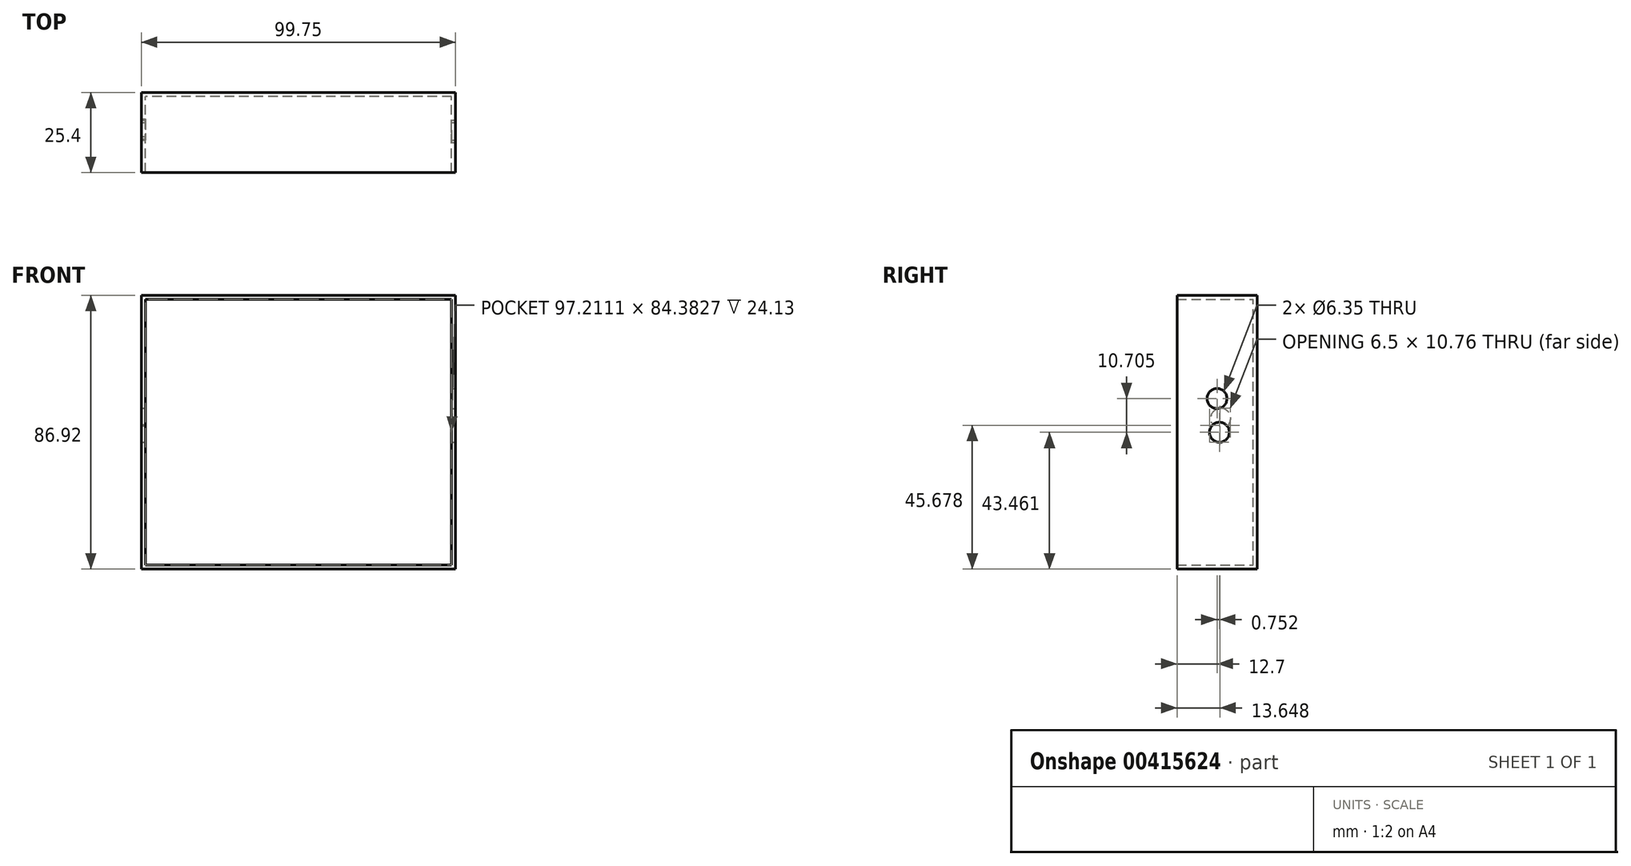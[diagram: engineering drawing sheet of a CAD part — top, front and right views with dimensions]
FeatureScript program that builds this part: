
annotation { "Feature Type Name" : "Feature", "Feature Type Description" : "" }
export const myFeature = defineFeature(function(context is Context, id is Id, definition is map)
    precondition{}
    {
        {
            var Q0;
            Q0=qCreatedBy(makeId("Front.planeOp"),FACE);
            var sketch = newSketch(context, id + "F0", { "sketchPlane" : qUnion([Q0])});
            skLineSegment(sketch, "E0.bottom", {"start": v(99.75, 0) * mm, "end": v(0, 0) * mm});
            skLineSegment(sketch, "E0.top", {"start": v(99.75, 86.92) * mm, "end": v(0, 86.92) * mm});
            skLineSegment(sketch, "E0.left", {"start": v(99.75, 0) * mm, "end": v(99.75, 86.92) * mm});
            skLineSegment(sketch, "E0.right", {"start": v(0, 0) * mm, "end": v(0, 86.92) * mm});
            skSolve(sketch);
        }
        {
            var Q0;
            Q0=makeQuery(id+"F0.imprint","IMPRINT",FACE,{"disambiguationData":[TD([[makeQuery(id+"F0.imprint","IMPRINT",EDGE,{"derivedFrom":sQuery(id+"F0.wireOp",EDGE,"E0.bottom")}),-1.0]])]});
            extrude(context, id + "F1", {"entities" : qUnion([Q0]), "depth" : 25.4 * mm});
        }
        {
            var Q0;
            Q0=makeQuery(id+"F1.opExtrude","CAP_FACE",FACE,{"disambiguationData":[OSD([sQuery(id+"F0.wireOp",EDGE,"E0.bottom"),sQuery(id+"F0.wireOp",EDGE,"E0.top"),sQuery(id+"F0.wireOp",EDGE,"E0.left"),sQuery(id+"F0.wireOp",EDGE,"E0.right")])],"isStart":false});
            shell(context, id + "F2", {"entities" : qUnion([Q0]), "thickness" : 1.27 * mm});
        }
        {
            var Q0;
            Q0=makeQuery(id+"F1.opExtrude","SWEPT_FACE",FACE,{"disambiguationData":[OSD([sQuery(id+"F0.wireOp",EDGE,"E0.left")])]});
            var sketch = newSketch(context, id + "F3", { "sketchPlane" : qUnion([Q0])});
            skPoint(sketch, "E1", {"position": v(-11.95, 43.46) * mm});
            skPoint(sketch, "E1.positionSnap0", {"position": v(0, 43.46) * mm});
            skSolve(sketch);
        }
        {
            var Q0;
            Q0=sQuery(id+"F3.wireOp",VERTEX,"E1");
            var Q1;
            Q1=makeQuery(id+"F1.opExtrude","SWEPT_BODY",BODY,{"disambiguationData":[OSD([sQuery(id+"F0.wireOp",EDGE,"E0.bottom"),sQuery(id+"F0.wireOp",EDGE,"E0.top"),sQuery(id+"F0.wireOp",EDGE,"E0.left"),sQuery(id+"F0.wireOp",EDGE,"E0.right")])]});
            hole(context, id + "F4", {"style" : HoleStyle.SIMPLE, "endStyle" : HoleEndStyle.THROUGH, "holeDiameter" : 6.35 * mm, "isTappedThrough" : true, "tappedDepth" : 12.7 * mm, "tapClearance" : 3, "locations" : qUnion([Q0]), "scope" : qUnion([Q1])});
        }
        {
            var Q0;
            Q0=makeQuery(id+"F2.opShell","OFFSET_FACE",FACE,{"disambiguationData":[OSD([sQuery(id+"F0.wireOp",EDGE,"E0.right")])]});
            var sketch = newSketch(context, id + "F5", { "sketchPlane" : qUnion([Q0])});
            skPoint(sketch, "E2", {"position": v(-11.56, 46.61) * mm});
            skPoint(sketch, "E3", {"position": v(-11.56, 47.9) * mm});
            skSolve(sketch);
        }
        {
            var Q0;
            Q0=sQuery(id+"F5.wireOp",VERTEX,"E3");
            var Q1;
            Q1=makeQuery(id+"F1.opExtrude","SWEPT_BODY",BODY,{"disambiguationData":[OSD([sQuery(id+"F0.wireOp",EDGE,"E0.bottom"),sQuery(id+"F0.wireOp",EDGE,"E0.top"),sQuery(id+"F0.wireOp",EDGE,"E0.left"),sQuery(id+"F0.wireOp",EDGE,"E0.right")])]});
            hole(context, id + "F6", {"style" : HoleStyle.SIMPLE, "endStyle" : HoleEndStyle.BLIND, "holeDiameter" : 6.35 * mm, "holeDepth" : 12.7 * mm, "isTappedThrough" : true, "tappedDepth" : 12.7 * mm, "tapClearance" : 3, "locations" : qUnion([Q0]), "scope" : qUnion([Q1])});
        }
        {
            var Q0;
            Q0=makeQuery(id+"F1.opExtrude","SWEPT_FACE",FACE,{"disambiguationData":[OSD([sQuery(id+"F0.wireOp",EDGE,"E0.left")])]});
            var sketch = newSketch(context, id + "F7", { "sketchPlane" : qUnion([Q0])});
            skPoint(sketch, "E4", {"position": v(-12.7, 54.17) * mm});
            skPoint(sketch, "E4.positionSnap0", {"position": v(-12.7, 86.92) * mm});
            skSolve(sketch);
        }
        {
            var Q0;
            Q0=sQuery(id+"F7.wireOp",VERTEX,"E4");
            var Q1;
            Q1=makeQuery(id+"F1.opExtrude","SWEPT_BODY",BODY,{"disambiguationData":[OSD([sQuery(id+"F0.wireOp",EDGE,"E0.bottom"),sQuery(id+"F0.wireOp",EDGE,"E0.top"),sQuery(id+"F0.wireOp",EDGE,"E0.left"),sQuery(id+"F0.wireOp",EDGE,"E0.right")])]});
            hole(context, id + "F8", {"style" : HoleStyle.SIMPLE, "endStyle" : HoleEndStyle.BLIND, "holeDiameter" : 6.35 * mm, "holeDepth" : 12.7 * mm, "isTappedThrough" : true, "tappedDepth" : 12.7 * mm, "tapClearance" : 3, "locations" : qUnion([Q0]), "scope" : qUnion([Q1])});
        }
    });
